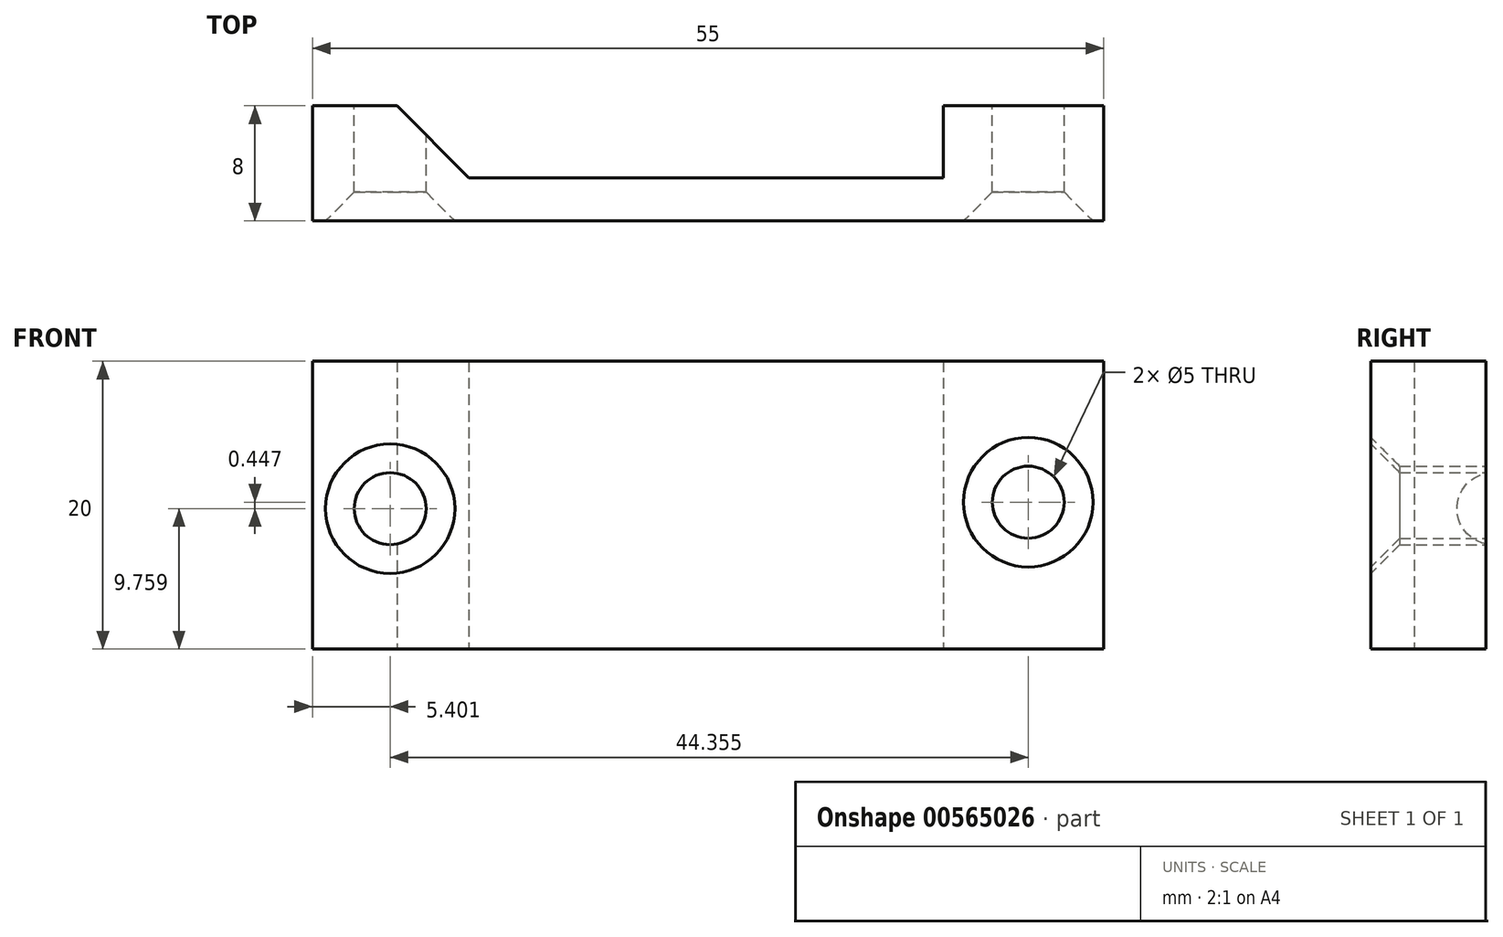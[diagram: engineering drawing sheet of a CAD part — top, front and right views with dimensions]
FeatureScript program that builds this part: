
annotation { "Feature Type Name" : "Feature", "Feature Type Description" : "" }
export const myFeature = defineFeature(function(context is Context, id is Id, definition is map)
    precondition{}
    {
        {
            var Q0;
            Q0=qCreatedBy(makeId("Top.planeOp"),FACE);
            var sketch = newSketch(context, id + "F0", { "sketchPlane" : qUnion([Q0])});
            skLineSegment(sketch, "E0.bottom", {"start": v(-61.95, -8) * mm, "end": v(-6.95, -8) * mm});
            skLineSegment(sketch, "E0.top", {"start": v(-61.95, 0) * mm, "end": v(-6.95, 0) * mm});
            skLineSegment(sketch, "E0.left", {"start": v(-61.95, -8) * mm, "end": v(-61.95, 0) * mm});
            skLineSegment(sketch, "E0.right", {"start": v(-6.95, -8) * mm, "end": v(-6.95, 0) * mm});
            skSolve(sketch);
        }
        {
            var Q0;
            Q0=makeQuery(id+"F0.imprint","IMPRINT",FACE,{"disambiguationData":[TD([[makeQuery(id+"F0.imprint","IMPRINT",EDGE,{"derivedFrom":sQuery(id+"F0.wireOp",EDGE,"E0.bottom")}),1.0]])]});
            extrude(context, id + "F1", {"entities" : qUnion([Q0]), "depth" : 20 * mm, "offsetDistance" : 25 * mm});
        }
        {
            var Q0;
            Q0=qCreatedBy(makeId("Front.planeOp"),FACE);
            var sketch = newSketch(context, id + "F2", { "sketchPlane" : qUnion([Q0])});
            skCircle(sketch, "E1", {"center": v(-56.55, 9.76) * mm, "radius": 2.5 * mm});
            skCircle(sketch, "E2", {"center": v(-12.2, 10.2) * mm, "radius": 2.5 * mm});
            skSolve(sketch);
        }
        {
            var Q0;
            Q0=qSketchRegion(id+"F2",true);
            extrude(context, id + "F3", {"entities" : qUnion([Q0]), "operationType" : NewBodyOperationType.REMOVE, "depth" : 35.3 * mm, "offsetDistance" : 25 * mm});
        }
        {
            var Q0;
            Q0=qCreatedBy(makeId("Front.planeOp"),FACE);
            var sketch = newSketch(context, id + "F4", { "sketchPlane" : qUnion([Q0])});
            skLineSegment(sketch, "E3.bottom", {"start": v(-51.08, 69.08) * mm, "end": v(-18.08, 69.08) * mm});
            skLineSegment(sketch, "E3.top", {"start": v(-51.08, -16.92) * mm, "end": v(-18.08, -16.92) * mm});
            skLineSegment(sketch, "E3.left", {"start": v(-51.08, 69.08) * mm, "end": v(-51.08, -16.92) * mm});
            skLineSegment(sketch, "E3.right", {"start": v(-18.08, 69.08) * mm, "end": v(-18.08, -16.92) * mm});
            skSolve(sketch);
        }
        {
            var Q0;
            Q0=qSketchRegion(id+"F4",true);
            extrude(context, id + "F5", {"entities" : qUnion([Q0]), "operationType" : NewBodyOperationType.REMOVE, "depth" : 5 * mm, "offsetDistance" : 25 * mm});
        }
        {
            var Q0;
            Q0=makeQuery(id+"F3.boolean.opBoolean","INTERSECT",EDGE,{"derivedFrom":[makeQuery(id+"F1.opExtrude","SWEPT_FACE",FACE,{"disambiguationData":[OSD([sQuery(id+"F0.wireOp",EDGE,"E0.bottom")])]}),makeQuery(id+"F3.opExtrude","SWEPT_FACE",FACE,{"disambiguationData":[OSD([sQuery(id+"F2.wireOp",EDGE,"E2")])]})]});
            chamfer(context, id + "F6", {"entities" : qUnion([Q0]), "width" : 2 * mm, "tangentPropagation" : true});
        }
        {
            var Q0;
            Q0=makeQuery(id+"F3.boolean.opBoolean","INTERSECT",EDGE,{"derivedFrom":[makeQuery(id+"F1.opExtrude","SWEPT_FACE",FACE,{"disambiguationData":[OSD([sQuery(id+"F0.wireOp",EDGE,"E0.bottom")])]}),makeQuery(id+"F3.opExtrude","SWEPT_FACE",FACE,{"disambiguationData":[OSD([sQuery(id+"F2.wireOp",EDGE,"E1")])]})]});
            chamfer(context, id + "F7", {"entities" : qUnion([Q0]), "width" : 2 * mm, "tangentPropagation" : true});
        }
        {
            var Q0;
            Q0=makeQuery(id+"F5.boolean.opBoolean","COPY",EDGE,{"derivedFrom":makeQuery(id+"F5.opExtrude","CAP_EDGE",EDGE,{"disambiguationData":[OSD([sQuery(id+"F4.wireOp",EDGE,"E3.left")])],"isStart":true})});
            var Q1;
            Q1=makeQuery(id+"F5.boolean.opBoolean","COPY",EDGE,{"derivedFrom":makeQuery(id+"F5.opExtrude","CAP_EDGE",EDGE,{"disambiguationData":[OSD([sQuery(id+"F4.wireOp",EDGE,"E3.right")])],"isStart":true})});
            chamfer(context, id + "F8", {"entities" : qUnion([Q0, Q1]), "width" : 5 * mm, "tangentPropagation" : true});
        }
    });
